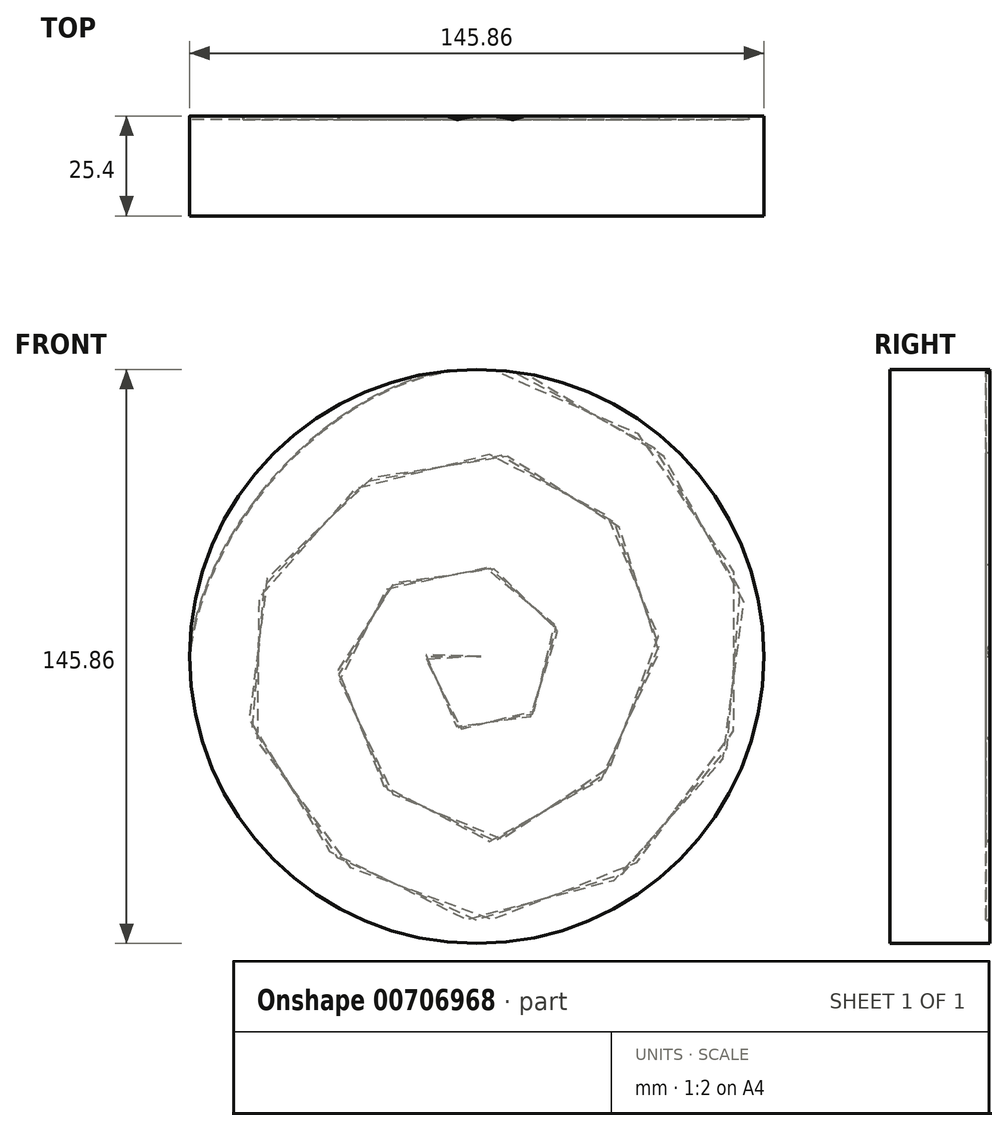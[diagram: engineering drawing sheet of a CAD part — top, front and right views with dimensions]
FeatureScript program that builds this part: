
annotation { "Feature Type Name" : "Feature", "Feature Type Description" : "" }
export const myFeature = defineFeature(function(context is Context, id is Id, definition is map)
    precondition{}
    {
        {
            var Q0;
            Q0=qCreatedBy(makeId("Front.planeOp"),FACE);
            var sketch = newSketch(context, id + "F0", { "sketchPlane" : qUnion([Q0])});
            skCircle(sketch, "E0", {"center": v(0, 0) * mm, "radius": 72.93 * mm});
            skSolve(sketch);
        }
        {
            var Q0;
            Q0=makeQuery(id+"F0.imprint","IMPRINT",FACE,{"disambiguationData":[TD([[makeQuery(id+"F0.imprint","IMPRINT",EDGE,{"derivedFrom":sQuery(id+"F0.wireOp",EDGE,"E0")}),1.0]])]});
            extrude(context, id + "F1", {"entities" : qUnion([Q0]), "depth" : 25.4 * mm, "offsetDistance" : 25.4 * mm});
        }
        {
            var Q0;
            Q0=makeQuery(id+"F1.opExtrude","CAP_FACE",FACE,{"disambiguationData":[OSD([sQuery(id+"F0.wireOp",EDGE,"E0")])],"isStart":true});
            var sketch = newSketch(context, id + "F2", { "sketchPlane" : qUnion([Q0])});
            skFitSpline(sketch, "E1", {"points": [v(0, 0) * mm, v(12.63, 0) * mm, v(0, -20.35) * mm, v(-20.82, 0) * mm, v(0, 22.9) * mm, v(34.53, 0) * mm, v(0, -46.6) * mm, v(-46.14, 3.55) * mm, v(0, 51.54) * mm, v(59.05, 0) * mm, v(0, -66.72) * mm, v(-68.96, 0) * mm, v(0, 72.93) * mm, v(72.93, 0) * mm, v(23.12, -82.88) * mm], "startDerivative": vector(515.2, 148.5) * mm, "endDerivative": vector(-870.86, -840.96) * mm});
            skSolve(sketch);
        }
        {
            var Q0;
            Q0=qCreatedBy(makeId("Top.planeOp"),FACE);
            var sketch = newSketch(context, id + "F3", { "sketchPlane" : qUnion([Q0])});
            skLineSegment(sketch, "E2", {"start": v(0, 0) * mm, "end": v(1.08, 0) * mm});
            skLineSegment(sketch, "E3", {"start": v(1.08, 0) * mm, "end": v(0.54, -0.93) * mm});
            skLineSegment(sketch, "E4", {"start": v(0.54, -0.93) * mm, "end": v(0, 0) * mm});
            skSolve(sketch);
        }
        {
            var Q0;
            Q0 = qSketchRegion(id + "F3", true);
            var Q1;
            Q1=sQuery(id+"F2.wireOp",EDGE,"E1");
            sweep(context, id + "F4", {"operationType" : NewBodyOperationType.REMOVE, "profiles" : qUnion([Q0]), "path" : qUnion([Q1])});
        }
    });
